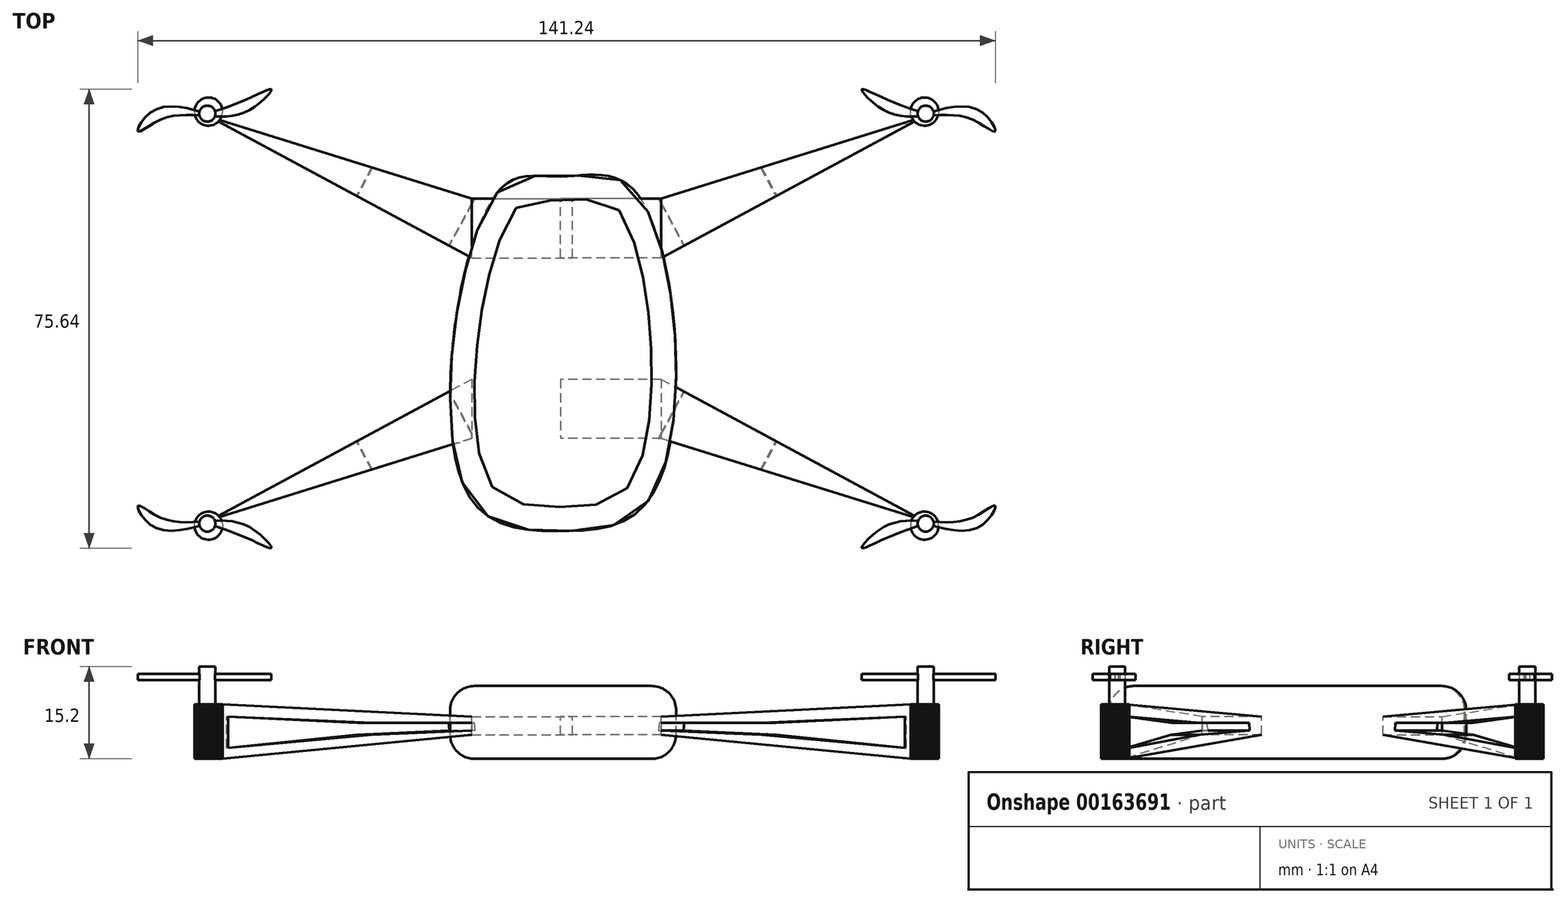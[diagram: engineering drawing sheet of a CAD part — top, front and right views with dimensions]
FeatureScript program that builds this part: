
annotation { "Feature Type Name" : "Feature", "Feature Type Description" : "" }
export const myFeature = defineFeature(function(context is Context, id is Id, definition is map)
    precondition{}
    {
        {
            var Q0;
            Q0=qCreatedBy(makeId("Top.planeOp"),FACE);
            var sketch = newSketch(context, id + "F0", { "sketchPlane" : qUnion([Q0])});
            skFitSpline(sketch, "E0", {"points": [v(-10.4, 10.8) * mm, v(0, 13.41) * mm, v(12.42, 10.8) * mm, v(15.84, -37.74) * mm, v(0, -45.01) * mm, v(-15.84, -37.74) * mm, v(-10.4, 10.8) * mm]});
            skLineSegment(sketch, "E1", {"start": v(-10.4, 10.8) * mm, "end": v(12.42, 10.8) * mm, "construction": true});
            skLineSegment(sketch, "E2", {"start": v(-15.84, -37.74) * mm, "end": v(15.84, -37.74) * mm, "construction": true});
            skSolve(sketch);
        }
        {
            var Q0;
            Q0=makeQuery(id+"F0.imprint","IMPRINT",FACE,{"disambiguationData":[TD([[makeQuery(id+"F0.imprint","IMPRINT",EDGE,{"derivedFrom":sQuery(id+"F0.wireOp",EDGE,"E0")}),-1.0]])]});
            extrude(context, id + "F1", {"entities" : qUnion([Q0]), "depth" : 12 * mm});
        }
        {
            var Q0;
            Q0=makeQuery(id+"F1.opExtrude","CAP_EDGE",EDGE,{"disambiguationData":[OSD([sQuery(id+"F0.wireOp",EDGE,"E0")])],"isStart":false});
            var Q1;
            Q1=makeQuery(id+"F1.opExtrude","CAP_EDGE",EDGE,{"disambiguationData":[OSD([sQuery(id+"F0.wireOp",EDGE,"E0")])],"isStart":true});
            fillet(context, id + "F2", {"entities" : qUnion([Q0, Q1]), "radius" : 4 * mm, "tangentPropagation" : true, "allowEdgeOverflow" : false});
        }
        {
            var Q0;
            Q0=qCreatedBy(makeId("Top.planeOp"),FACE);
            var sketch = newSketch(context, id + "F3", { "sketchPlane" : qUnion([Q0])});
            skCircle(sketch, "E3.cCircle", {"center": v(59.95, 24.1) * mm, "radius": 2.31 * mm, "construction": true});
            skLineSegment(sketch, "E3.0", {"start": v(58.44, 25.86) * mm, "end": v(58.67, 26.04) * mm});
            skLineSegment(sketch, "E3.1", {"start": v(58.67, 26.04) * mm, "end": v(58.92, 26.18) * mm});
            skLineSegment(sketch, "E3.2", {"start": v(58.92, 26.18) * mm, "end": v(59.19, 26.3) * mm});
            skLineSegment(sketch, "E3.3", {"start": v(59.19, 26.3) * mm, "end": v(59.47, 26.38) * mm});
            skLineSegment(sketch, "E3.4", {"start": v(59.47, 26.38) * mm, "end": v(59.76, 26.42) * mm});
            skLineSegment(sketch, "E3.5", {"start": v(59.76, 26.42) * mm, "end": v(60.05, 26.43) * mm});
            skLineSegment(sketch, "E3.6", {"start": v(60.05, 26.43) * mm, "end": v(60.34, 26.4) * mm});
            skLineSegment(sketch, "E3.7", {"start": v(60.34, 26.4) * mm, "end": v(60.62, 26.33) * mm});
            skLineSegment(sketch, "E3.8", {"start": v(60.62, 26.33) * mm, "end": v(60.9, 26.23) * mm});
            skLineSegment(sketch, "E3.9", {"start": v(60.9, 26.23) * mm, "end": v(61.15, 26.1) * mm});
            skLineSegment(sketch, "E3.10", {"start": v(61.15, 26.1) * mm, "end": v(61.39, 25.93) * mm});
            skLineSegment(sketch, "E3.11", {"start": v(61.39, 25.93) * mm, "end": v(61.6, 25.73) * mm});
            skLineSegment(sketch, "E3.12", {"start": v(61.6, 25.73) * mm, "end": v(61.8, 25.51) * mm});
            skLineSegment(sketch, "E3.13", {"start": v(61.8, 25.51) * mm, "end": v(61.96, 25.27) * mm});
            skLineSegment(sketch, "E3.14", {"start": v(61.96, 25.27) * mm, "end": v(62.09, 25) * mm});
            skLineSegment(sketch, "E3.15", {"start": v(62.09, 25) * mm, "end": v(62.18, 24.73) * mm});
            skLineSegment(sketch, "E3.16", {"start": v(62.18, 24.73) * mm, "end": v(62.24, 24.45) * mm});
            skLineSegment(sketch, "E3.17", {"start": v(62.24, 24.45) * mm, "end": v(62.27, 24.16) * mm});
            skLineSegment(sketch, "E3.18", {"start": v(62.27, 24.16) * mm, "end": v(62.26, 23.87) * mm});
            skLineSegment(sketch, "E3.19", {"start": v(62.26, 23.87) * mm, "end": v(62.2, 23.58) * mm});
            skLineSegment(sketch, "E3.20", {"start": v(62.2, 23.58) * mm, "end": v(62.12, 23.3) * mm});
            skLineSegment(sketch, "E3.21", {"start": v(62.12, 23.3) * mm, "end": v(62, 23.04) * mm});
            skLineSegment(sketch, "E3.22", {"start": v(62, 23.04) * mm, "end": v(61.85, 22.79) * mm});
            skLineSegment(sketch, "E3.23", {"start": v(61.85, 22.79) * mm, "end": v(61.67, 22.56) * mm});
            skLineSegment(sketch, "E3.24", {"start": v(61.67, 22.56) * mm, "end": v(61.47, 22.35) * mm});
            skLineSegment(sketch, "E3.25", {"start": v(61.47, 22.35) * mm, "end": v(61.23, 22.18) * mm});
            skLineSegment(sketch, "E3.26", {"start": v(61.23, 22.18) * mm, "end": v(60.98, 22.03) * mm});
            skLineSegment(sketch, "E3.27", {"start": v(60.98, 22.03) * mm, "end": v(60.71, 21.92) * mm});
            skLineSegment(sketch, "E3.28", {"start": v(60.71, 21.92) * mm, "end": v(60.43, 21.84) * mm});
            skLineSegment(sketch, "E3.29", {"start": v(60.43, 21.84) * mm, "end": v(60.15, 21.8) * mm});
            skLineSegment(sketch, "E3.30", {"start": v(60.15, 21.8) * mm, "end": v(59.85, 21.8) * mm});
            skLineSegment(sketch, "E3.31", {"start": v(59.85, 21.8) * mm, "end": v(59.56, 21.82) * mm});
            skLineSegment(sketch, "E3.32", {"start": v(59.56, 21.82) * mm, "end": v(59.28, 21.89) * mm});
            skLineSegment(sketch, "E3.33", {"start": v(59.28, 21.89) * mm, "end": v(59, 22) * mm});
            skLineSegment(sketch, "E3.34", {"start": v(59, 22) * mm, "end": v(58.75, 22.13) * mm});
            skLineSegment(sketch, "E3.35", {"start": v(58.75, 22.13) * mm, "end": v(58.51, 22.3) * mm});
            skLineSegment(sketch, "E3.36", {"start": v(58.51, 22.3) * mm, "end": v(58.3, 22.49) * mm});
            skLineSegment(sketch, "E3.37", {"start": v(58.3, 22.49) * mm, "end": v(58.1, 22.7) * mm});
            skLineSegment(sketch, "E3.38", {"start": v(58.1, 22.7) * mm, "end": v(57.94, 22.95) * mm});
            skLineSegment(sketch, "E3.39", {"start": v(57.94, 22.95) * mm, "end": v(57.81, 23.2) * mm});
            skLineSegment(sketch, "E3.40", {"start": v(57.81, 23.2) * mm, "end": v(57.72, 23.48) * mm});
            skLineSegment(sketch, "E3.41", {"start": v(57.72, 23.48) * mm, "end": v(57.66, 23.77) * mm});
            skLineSegment(sketch, "E3.42", {"start": v(57.66, 23.77) * mm, "end": v(57.63, 24.06) * mm});
            skLineSegment(sketch, "E3.43", {"start": v(57.63, 24.06) * mm, "end": v(57.65, 24.35) * mm});
            skLineSegment(sketch, "E3.44", {"start": v(57.65, 24.35) * mm, "end": v(57.7, 24.64) * mm});
            skLineSegment(sketch, "E3.45", {"start": v(57.7, 24.64) * mm, "end": v(57.78, 24.92) * mm});
            skLineSegment(sketch, "E3.46", {"start": v(57.78, 24.92) * mm, "end": v(57.9, 25.18) * mm});
            skLineSegment(sketch, "E3.47", {"start": v(57.9, 25.18) * mm, "end": v(58.05, 25.43) * mm});
            skLineSegment(sketch, "E3.48", {"start": v(58.05, 25.43) * mm, "end": v(58.23, 25.66) * mm});
            skLineSegment(sketch, "E3.49", {"start": v(58.23, 25.66) * mm, "end": v(58.44, 25.86) * mm});
            skPoint(sketch, "E3.0.midPoint", {"position": v(58.55, 25.95) * mm});
            skSolve(sketch);
        }
        {
            var Q0;
            Q0 = qSketchRegion(id + "F3", true);
            extrude(context, id + "F4", {"entities" : qUnion([Q0]), "depth" : 9 * mm});
        }
        {
            var Q0;
            Q0=makeQuery(id+"F4.opExtrude","CAP_FACE",FACE,{"disambiguationData":[OSD([sQuery(id+"F3.wireOp",EDGE,"E3.0"),sQuery(id+"F3.wireOp",EDGE,"E3.1"),sQuery(id+"F3.wireOp",EDGE,"E3.2"),sQuery(id+"F3.wireOp",EDGE,"E3.3"),sQuery(id+"F3.wireOp",EDGE,"E3.4"),sQuery(id+"F3.wireOp",EDGE,"E3.5"),sQuery(id+"F3.wireOp",EDGE,"E3.6"),sQuery(id+"F3.wireOp",EDGE,"E3.7"),sQuery(id+"F3.wireOp",EDGE,"E3.8"),sQuery(id+"F3.wireOp",EDGE,"E3.9"),sQuery(id+"F3.wireOp",EDGE,"E3.10"),sQuery(id+"F3.wireOp",EDGE,"E3.11"),sQuery(id+"F3.wireOp",EDGE,"E3.12"),sQuery(id+"F3.wireOp",EDGE,"E3.13"),sQuery(id+"F3.wireOp",EDGE,"E3.14"),sQuery(id+"F3.wireOp",EDGE,"E3.15"),sQuery(id+"F3.wireOp",EDGE,"E3.16"),sQuery(id+"F3.wireOp",EDGE,"E3.17"),sQuery(id+"F3.wireOp",EDGE,"E3.18"),sQuery(id+"F3.wireOp",EDGE,"E3.19"),sQuery(id+"F3.wireOp",EDGE,"E3.20"),sQuery(id+"F3.wireOp",EDGE,"E3.21"),sQuery(id+"F3.wireOp",EDGE,"E3.22"),sQuery(id+"F3.wireOp",EDGE,"E3.23"),sQuery(id+"F3.wireOp",EDGE,"E3.24"),sQuery(id+"F3.wireOp",EDGE,"E3.25"),sQuery(id+"F3.wireOp",EDGE,"E3.26"),sQuery(id+"F3.wireOp",EDGE,"E3.27"),sQuery(id+"F3.wireOp",EDGE,"E3.28"),sQuery(id+"F3.wireOp",EDGE,"E3.29"),sQuery(id+"F3.wireOp",EDGE,"E3.30"),sQuery(id+"F3.wireOp",EDGE,"E3.31"),sQuery(id+"F3.wireOp",EDGE,"E3.32"),sQuery(id+"F3.wireOp",EDGE,"E3.33"),sQuery(id+"F3.wireOp",EDGE,"E3.34"),sQuery(id+"F3.wireOp",EDGE,"E3.35"),sQuery(id+"F3.wireOp",EDGE,"E3.36"),sQuery(id+"F3.wireOp",EDGE,"E3.37"),sQuery(id+"F3.wireOp",EDGE,"E3.38"),sQuery(id+"F3.wireOp",EDGE,"E3.39"),sQuery(id+"F3.wireOp",EDGE,"E3.40"),sQuery(id+"F3.wireOp",EDGE,"E3.41"),sQuery(id+"F3.wireOp",EDGE,"E3.42"),sQuery(id+"F3.wireOp",EDGE,"E3.43"),sQuery(id+"F3.wireOp",EDGE,"E3.44"),sQuery(id+"F3.wireOp",EDGE,"E3.45"),sQuery(id+"F3.wireOp",EDGE,"E3.46"),sQuery(id+"F3.wireOp",EDGE,"E3.47"),sQuery(id+"F3.wireOp",EDGE,"E3.48"),sQuery(id+"F3.wireOp",EDGE,"E3.49")])],"isStart":false});
            var sketch = newSketch(context, id + "F5", { "sketchPlane" : qUnion([Q0])});
            skCircle(sketch, "E4", {"center": v(60.15, 23.77) * mm, "radius": 1.33 * mm});
            skSolve(sketch);
        }
        {
            var Q0;
            Q0 = qSketchRegion(id + "F5", true);
            extrude(context, id + "F6", {"entities" : qUnion([Q0]), "operationType" : NewBodyOperationType.ADD, "depth" : 6.2 * mm});
        }
        {
            var Q0;
            Q0=qCreatedBy(makeId("Top.planeOp"),FACE);
            cPlane(context, id + "F7", {"entities" : qUnion([Q0]), "cplaneType" : CPlaneType.OFFSET, "offset" : 13 * mm, "width" : 150 * mm, "height" : 150 * mm});
        }
        {
            var Q0;
            Q0=qCreatedBy(id+"F7.planeOp",FACE);
            var sketch = newSketch(context, id + "F8", { "sketchPlane" : qUnion([Q0])});
            skFitSpline(sketch, "E5", {"points": [v(59.79, 23.87) * mm, v(53.3, 26.3) * mm, v(49.6, 27.75) * mm, v(53.2, 24.37) * mm, v(60.08, 23.36) * mm, v(67.82, 22.8) * mm, v(71.57, 20.83) * mm, v(68.5, 24.52) * mm, v(60.5, 23.87) * mm, v(59.79, 23.87) * mm]});
            skSolve(sketch);
        }
        {
            var Q0;
            Q0=makeQuery(id+"F8.imprint","IMPRINT",FACE,{"disambiguationData":[TD([[makeQuery(id+"F8.imprint","IMPRINT",EDGE,{"derivedFrom":sQuery(id+"F8.wireOp",EDGE,"E5")}),1.0]])]});
            extrude(context, id + "F9", {"entities" : qUnion([Q0]), "operationType" : NewBodyOperationType.ADD, "depth" : 1 * mm});
        }
        {
            var Q0;
            Q0=qCreatedBy(makeId("Right.planeOp"),FACE);
            var sketch = newSketch(context, id + "F10", { "sketchPlane" : qUnion([Q0])});
            skLineSegment(sketch, "E6.bottom", {"start": v(0, 3.99) * mm, "end": v(9.74, 3.99) * mm});
            skLineSegment(sketch, "E6.top", {"start": v(0, 6.96) * mm, "end": v(9.74, 6.96) * mm});
            skLineSegment(sketch, "E6.left", {"start": v(0, 3.99) * mm, "end": v(0, 6.96) * mm});
            skLineSegment(sketch, "E6.right", {"start": v(9.74, 3.99) * mm, "end": v(9.74, 6.96) * mm});
            skSolve(sketch);
        }
        {
            var Q0;
            Q0 = qSketchRegion(id + "F10", true);
            extrude(context, id + "F11", {"entities" : qUnion([Q0]), "depth" : 16.6 * mm});
        }
        {
            var Q0;
            Q0=makeQuery(id+"F11.opExtrude","CAP_FACE",FACE,{"disambiguationData":[OSD([sQuery(id+"F10.wireOp",EDGE,"E6.bottom"),sQuery(id+"F10.wireOp",EDGE,"E6.top"),sQuery(id+"F10.wireOp",EDGE,"E6.left"),sQuery(id+"F10.wireOp",EDGE,"E6.right")])],"isStart":false});
            var Q1;
            Q1=makeQuery(id+"F4.opExtrude","SWEPT_FACE",FACE,{"disambiguationData":[OSD([sQuery(id+"F3.wireOp",EDGE,"E3.37")])]});
            loft(context, id + "F12", {"sheetProfilesArray" : [{ "sheetProfileEntities" : qUnion([Q0]) }, { "sheetProfileEntities" : qUnion([Q1]) }]});
        }
        {
            var Q0;
            Q0=qCreatedBy(makeId("Front.planeOp"),FACE);
            cPlane(context, id + "F13", {"entities" : qUnion([Q0]), "cplaneType" : CPlaneType.OFFSET, "offset" : 10 * mm, "width" : 150 * mm, "height" : 150 * mm});
        }
        {
            var Q0;
            Q0=qCreatedBy(makeId("Right.planeOp"),FACE);
            cPlane(context, id + "F14", {"entities" : qUnion([Q0]), "cplaneType" : CPlaneType.OFFSET, "offset" : 1 * mm, "width" : 150 * mm, "height" : 150 * mm});
        }
        {
            var Q0;
            Q0=makeQuery(id+"F12.opLoft","SWEPT_FACE",FACE,{"disambiguationData":[OSD([sQuery(id+"F3.wireOp",EDGE,"E3.36"),sQuery(id+"F3.wireOp",EDGE,"E3.37"),sQuery(id+"F10.wireOp",EDGE,"E6.bottom"),sQuery(id+"F10.wireOp",EDGE,"E6.top"),sQuery(id+"F10.wireOp",EDGE,"E6.left")])]});
            var sketch = newSketch(context, id + "F15", { "sketchPlane" : qUnion([Q0])});
            skLineSegment(sketch, "E7", {"start": v(18.91, 5.96) * mm, "end": v(18.8, 4.69) * mm});
            skLineSegment(sketch, "E8", {"start": v(18.8, 4.69) * mm, "end": v(36.21, 3.99) * mm});
            skLineSegment(sketch, "E9", {"start": v(36.21, 3.99) * mm, "end": v(60.5, 1.8) * mm});
            skLineSegment(sketch, "E10", {"start": v(60.5, 1.8) * mm, "end": v(60.5, 6.96) * mm});
            skLineSegment(sketch, "E11", {"start": v(60.5, 6.96) * mm, "end": v(36.05, 5.9) * mm});
            skLineSegment(sketch, "E12", {"start": v(36.05, 5.9) * mm, "end": v(18.91, 5.96) * mm});
            skSolve(sketch);
        }
        {
            var Q0;
            Q0 = qSketchRegion(id + "F15", true);
            extrude(context, id + "F16", {"entities" : qUnion([Q0]), "operationType" : NewBodyOperationType.REMOVE, "oppositeDirection" : true, "depth" : 10 * mm});
        }
        {
            var Q0;
            Q0=makeQuery(id+"F12.opLoft","SWEPT_BODY",BODY,{"disambiguationData":[OSD([sQuery(id+"F3.wireOp",EDGE,"E3.37"),sQuery(id+"F10.wireOp",EDGE,"E6.bottom"),sQuery(id+"F10.wireOp",EDGE,"E6.top"),sQuery(id+"F10.wireOp",EDGE,"E6.left"),sQuery(id+"F10.wireOp",EDGE,"E6.right")])]});
            var Q1;
            Q1=makeQuery(id+"F11.opExtrude","SWEPT_BODY",BODY,{"disambiguationData":[OSD([sQuery(id+"F10.wireOp",EDGE,"E6.bottom"),sQuery(id+"F10.wireOp",EDGE,"E6.top"),sQuery(id+"F10.wireOp",EDGE,"E6.left"),sQuery(id+"F10.wireOp",EDGE,"E6.right")])]});
            var Q2;
            Q2=makeQuery(id+"F4.opExtrude","SWEPT_BODY",BODY,{"disambiguationData":[OSD([sQuery(id+"F3.wireOp",EDGE,"E3.0"),sQuery(id+"F3.wireOp",EDGE,"E3.1"),sQuery(id+"F3.wireOp",EDGE,"E3.2"),sQuery(id+"F3.wireOp",EDGE,"E3.3"),sQuery(id+"F3.wireOp",EDGE,"E3.4"),sQuery(id+"F3.wireOp",EDGE,"E3.5"),sQuery(id+"F3.wireOp",EDGE,"E3.6"),sQuery(id+"F3.wireOp",EDGE,"E3.7"),sQuery(id+"F3.wireOp",EDGE,"E3.8"),sQuery(id+"F3.wireOp",EDGE,"E3.9"),sQuery(id+"F3.wireOp",EDGE,"E3.10"),sQuery(id+"F3.wireOp",EDGE,"E3.11"),sQuery(id+"F3.wireOp",EDGE,"E3.12"),sQuery(id+"F3.wireOp",EDGE,"E3.13"),sQuery(id+"F3.wireOp",EDGE,"E3.14"),sQuery(id+"F3.wireOp",EDGE,"E3.15"),sQuery(id+"F3.wireOp",EDGE,"E3.16"),sQuery(id+"F3.wireOp",EDGE,"E3.17"),sQuery(id+"F3.wireOp",EDGE,"E3.18"),sQuery(id+"F3.wireOp",EDGE,"E3.19"),sQuery(id+"F3.wireOp",EDGE,"E3.20"),sQuery(id+"F3.wireOp",EDGE,"E3.21"),sQuery(id+"F3.wireOp",EDGE,"E3.22"),sQuery(id+"F3.wireOp",EDGE,"E3.23"),sQuery(id+"F3.wireOp",EDGE,"E3.24"),sQuery(id+"F3.wireOp",EDGE,"E3.25"),sQuery(id+"F3.wireOp",EDGE,"E3.26"),sQuery(id+"F3.wireOp",EDGE,"E3.27"),sQuery(id+"F3.wireOp",EDGE,"E3.28"),sQuery(id+"F3.wireOp",EDGE,"E3.29"),sQuery(id+"F3.wireOp",EDGE,"E3.30"),sQuery(id+"F3.wireOp",EDGE,"E3.31"),sQuery(id+"F3.wireOp",EDGE,"E3.32"),sQuery(id+"F3.wireOp",EDGE,"E3.33"),sQuery(id+"F3.wireOp",EDGE,"E3.34"),sQuery(id+"F3.wireOp",EDGE,"E3.35"),sQuery(id+"F3.wireOp",EDGE,"E3.36"),sQuery(id+"F3.wireOp",EDGE,"E3.37"),sQuery(id+"F3.wireOp",EDGE,"E3.38"),sQuery(id+"F3.wireOp",EDGE,"E3.39"),sQuery(id+"F3.wireOp",EDGE,"E3.40"),sQuery(id+"F3.wireOp",EDGE,"E3.41"),sQuery(id+"F3.wireOp",EDGE,"E3.42"),sQuery(id+"F3.wireOp",EDGE,"E3.43"),sQuery(id+"F3.wireOp",EDGE,"E3.44"),sQuery(id+"F3.wireOp",EDGE,"E3.45"),sQuery(id+"F3.wireOp",EDGE,"E3.46"),sQuery(id+"F3.wireOp",EDGE,"E3.47"),sQuery(id+"F3.wireOp",EDGE,"E3.48"),sQuery(id+"F3.wireOp",EDGE,"E3.49")])]});
            var Q3;
            Q3=qCreatedBy(id+"F14.planeOp",FACE);
            mirror(context, id + "F17", {"entities" : qUnion([Q0, Q1, Q2]), "mirrorPlane" : qUnion([Q3])});
        }
        {
            var Q0;
            Q0=makeQuery(id+"F17.opPattern","COPY",BODY,{"derivedFrom":makeQuery(id+"F12.opLoft","SWEPT_BODY",BODY,{"disambiguationData":[OSD([sQuery(id+"F3.wireOp",EDGE,"E3.37"),sQuery(id+"F10.wireOp",EDGE,"E6.bottom"),sQuery(id+"F10.wireOp",EDGE,"E6.top"),sQuery(id+"F10.wireOp",EDGE,"E6.left"),sQuery(id+"F10.wireOp",EDGE,"E6.right")])]}),"instanceName":"1"});
            var Q1;
            Q1=makeQuery(id+"F12.opLoft","SWEPT_BODY",BODY,{"disambiguationData":[OSD([sQuery(id+"F3.wireOp",EDGE,"E3.37"),sQuery(id+"F10.wireOp",EDGE,"E6.bottom"),sQuery(id+"F10.wireOp",EDGE,"E6.top"),sQuery(id+"F10.wireOp",EDGE,"E6.left"),sQuery(id+"F10.wireOp",EDGE,"E6.right")])]});
            var Q2;
            Q2=makeQuery(id+"F11.opExtrude","SWEPT_BODY",BODY,{"disambiguationData":[OSD([sQuery(id+"F10.wireOp",EDGE,"E6.bottom"),sQuery(id+"F10.wireOp",EDGE,"E6.top"),sQuery(id+"F10.wireOp",EDGE,"E6.left"),sQuery(id+"F10.wireOp",EDGE,"E6.right")])]});
            var Q3;
            Q3=makeQuery(id+"F4.opExtrude","SWEPT_BODY",BODY,{"disambiguationData":[OSD([sQuery(id+"F3.wireOp",EDGE,"E3.0"),sQuery(id+"F3.wireOp",EDGE,"E3.1"),sQuery(id+"F3.wireOp",EDGE,"E3.2"),sQuery(id+"F3.wireOp",EDGE,"E3.3"),sQuery(id+"F3.wireOp",EDGE,"E3.4"),sQuery(id+"F3.wireOp",EDGE,"E3.5"),sQuery(id+"F3.wireOp",EDGE,"E3.6"),sQuery(id+"F3.wireOp",EDGE,"E3.7"),sQuery(id+"F3.wireOp",EDGE,"E3.8"),sQuery(id+"F3.wireOp",EDGE,"E3.9"),sQuery(id+"F3.wireOp",EDGE,"E3.10"),sQuery(id+"F3.wireOp",EDGE,"E3.11"),sQuery(id+"F3.wireOp",EDGE,"E3.12"),sQuery(id+"F3.wireOp",EDGE,"E3.13"),sQuery(id+"F3.wireOp",EDGE,"E3.14"),sQuery(id+"F3.wireOp",EDGE,"E3.15"),sQuery(id+"F3.wireOp",EDGE,"E3.16"),sQuery(id+"F3.wireOp",EDGE,"E3.17"),sQuery(id+"F3.wireOp",EDGE,"E3.18"),sQuery(id+"F3.wireOp",EDGE,"E3.19"),sQuery(id+"F3.wireOp",EDGE,"E3.20"),sQuery(id+"F3.wireOp",EDGE,"E3.21"),sQuery(id+"F3.wireOp",EDGE,"E3.22"),sQuery(id+"F3.wireOp",EDGE,"E3.23"),sQuery(id+"F3.wireOp",EDGE,"E3.24"),sQuery(id+"F3.wireOp",EDGE,"E3.25"),sQuery(id+"F3.wireOp",EDGE,"E3.26"),sQuery(id+"F3.wireOp",EDGE,"E3.27"),sQuery(id+"F3.wireOp",EDGE,"E3.28"),sQuery(id+"F3.wireOp",EDGE,"E3.29"),sQuery(id+"F3.wireOp",EDGE,"E3.30"),sQuery(id+"F3.wireOp",EDGE,"E3.31"),sQuery(id+"F3.wireOp",EDGE,"E3.32"),sQuery(id+"F3.wireOp",EDGE,"E3.33"),sQuery(id+"F3.wireOp",EDGE,"E3.34"),sQuery(id+"F3.wireOp",EDGE,"E3.35"),sQuery(id+"F3.wireOp",EDGE,"E3.36"),sQuery(id+"F3.wireOp",EDGE,"E3.37"),sQuery(id+"F3.wireOp",EDGE,"E3.38"),sQuery(id+"F3.wireOp",EDGE,"E3.39"),sQuery(id+"F3.wireOp",EDGE,"E3.40"),sQuery(id+"F3.wireOp",EDGE,"E3.41"),sQuery(id+"F3.wireOp",EDGE,"E3.42"),sQuery(id+"F3.wireOp",EDGE,"E3.43"),sQuery(id+"F3.wireOp",EDGE,"E3.44"),sQuery(id+"F3.wireOp",EDGE,"E3.45"),sQuery(id+"F3.wireOp",EDGE,"E3.46"),sQuery(id+"F3.wireOp",EDGE,"E3.47"),sQuery(id+"F3.wireOp",EDGE,"E3.48"),sQuery(id+"F3.wireOp",EDGE,"E3.49")])]});
            var Q4;
            Q4=makeQuery(id+"F17.opPattern","COPY",BODY,{"derivedFrom":makeQuery(id+"F4.opExtrude","SWEPT_BODY",BODY,{"disambiguationData":[OSD([sQuery(id+"F3.wireOp",EDGE,"E3.0"),sQuery(id+"F3.wireOp",EDGE,"E3.1"),sQuery(id+"F3.wireOp",EDGE,"E3.2"),sQuery(id+"F3.wireOp",EDGE,"E3.3"),sQuery(id+"F3.wireOp",EDGE,"E3.4"),sQuery(id+"F3.wireOp",EDGE,"E3.5"),sQuery(id+"F3.wireOp",EDGE,"E3.6"),sQuery(id+"F3.wireOp",EDGE,"E3.7"),sQuery(id+"F3.wireOp",EDGE,"E3.8"),sQuery(id+"F3.wireOp",EDGE,"E3.9"),sQuery(id+"F3.wireOp",EDGE,"E3.10"),sQuery(id+"F3.wireOp",EDGE,"E3.11"),sQuery(id+"F3.wireOp",EDGE,"E3.12"),sQuery(id+"F3.wireOp",EDGE,"E3.13"),sQuery(id+"F3.wireOp",EDGE,"E3.14"),sQuery(id+"F3.wireOp",EDGE,"E3.15"),sQuery(id+"F3.wireOp",EDGE,"E3.16"),sQuery(id+"F3.wireOp",EDGE,"E3.17"),sQuery(id+"F3.wireOp",EDGE,"E3.18"),sQuery(id+"F3.wireOp",EDGE,"E3.19"),sQuery(id+"F3.wireOp",EDGE,"E3.20"),sQuery(id+"F3.wireOp",EDGE,"E3.21"),sQuery(id+"F3.wireOp",EDGE,"E3.22"),sQuery(id+"F3.wireOp",EDGE,"E3.23"),sQuery(id+"F3.wireOp",EDGE,"E3.24"),sQuery(id+"F3.wireOp",EDGE,"E3.25"),sQuery(id+"F3.wireOp",EDGE,"E3.26"),sQuery(id+"F3.wireOp",EDGE,"E3.27"),sQuery(id+"F3.wireOp",EDGE,"E3.28"),sQuery(id+"F3.wireOp",EDGE,"E3.29"),sQuery(id+"F3.wireOp",EDGE,"E3.30"),sQuery(id+"F3.wireOp",EDGE,"E3.31"),sQuery(id+"F3.wireOp",EDGE,"E3.32"),sQuery(id+"F3.wireOp",EDGE,"E3.33"),sQuery(id+"F3.wireOp",EDGE,"E3.34"),sQuery(id+"F3.wireOp",EDGE,"E3.35"),sQuery(id+"F3.wireOp",EDGE,"E3.36"),sQuery(id+"F3.wireOp",EDGE,"E3.37"),sQuery(id+"F3.wireOp",EDGE,"E3.38"),sQuery(id+"F3.wireOp",EDGE,"E3.39"),sQuery(id+"F3.wireOp",EDGE,"E3.40"),sQuery(id+"F3.wireOp",EDGE,"E3.41"),sQuery(id+"F3.wireOp",EDGE,"E3.42"),sQuery(id+"F3.wireOp",EDGE,"E3.43"),sQuery(id+"F3.wireOp",EDGE,"E3.44"),sQuery(id+"F3.wireOp",EDGE,"E3.45"),sQuery(id+"F3.wireOp",EDGE,"E3.46"),sQuery(id+"F3.wireOp",EDGE,"E3.47"),sQuery(id+"F3.wireOp",EDGE,"E3.48"),sQuery(id+"F3.wireOp",EDGE,"E3.49")])]}),"instanceName":"1"});
            var Q5;
            Q5=qCreatedBy(id+"F13.planeOp",FACE);
            mirror(context, id + "F18", {"entities" : qUnion([Q0, Q1, Q2, Q3, Q4]), "mirrorPlane" : qUnion([Q5])});
        }
    });
